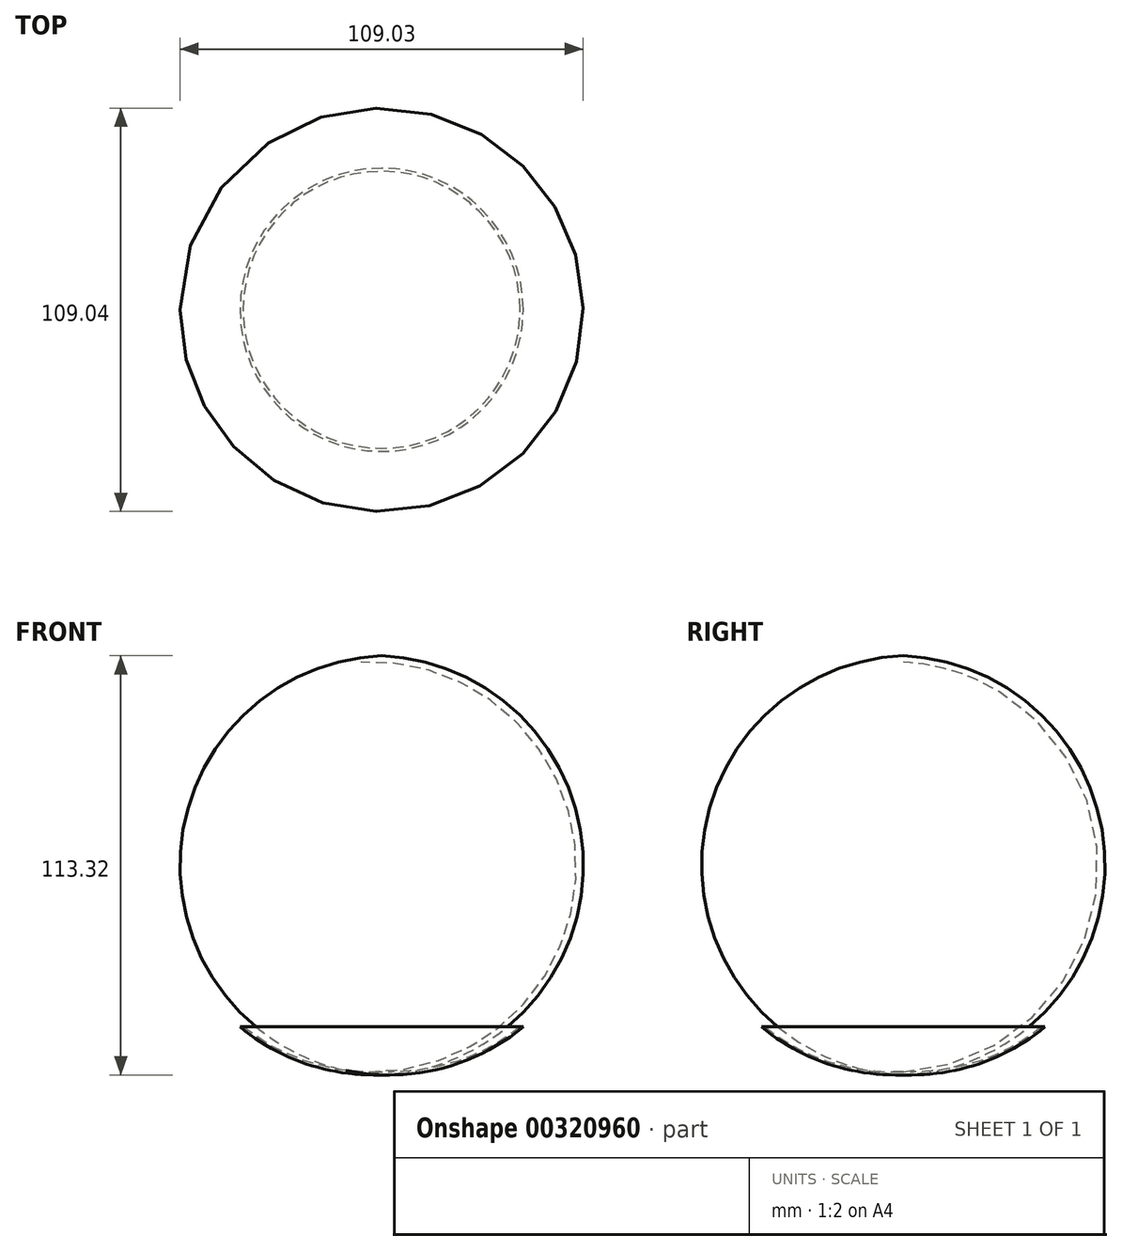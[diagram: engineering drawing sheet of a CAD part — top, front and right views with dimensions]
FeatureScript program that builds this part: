
annotation { "Feature Type Name" : "Feature", "Feature Type Description" : "" }
export const myFeature = defineFeature(function(context is Context, id is Id, definition is map)
    precondition{}
    {
        {
            var Q0;
            Q0=qCreatedBy(makeId("Front.planeOp"),FACE);
            var sketch = newSketch(context, id + "F0", { "sketchPlane" : qUnion([Q0])});
            skLineSegment(sketch, "E0", {"start": v(-76.27, 0) * mm, "end": v(-38, 0) * mm});
            skLineSegment(sketch, "E1", {"start": v(-38, 0) * mm, "end": v(-38, -12.95) * mm});
            skArc(sketch, "E2", {"start": v(-76.27, 0) * mm, "mid": v(-58.32, -10) * mm, "end": v(-38, -12.95) * mm});
            skSolve(sketch);
        }
        {
            var Q0;
            Q0 = qSketchRegion(id + "F0", true);
            var Q1;
            Q1=sQuery(id+"F0.wireOp",EDGE,"E1");
            revolve(context, id + "F1", {"entities" : qUnion([Q0]), "axis" : qUnion([Q1]), "revolveType" : RevolveType.FULL});
        }
        {
            var Q0;
            Q0=qCreatedBy(makeId("Front.planeOp"),FACE);
            var sketch = newSketch(context, id + "F2", { "sketchPlane" : qUnion([Q0])});
            skLineSegment(sketch, "E3", {"start": v(-38.02, 0) * mm, "end": v(-38.02, -12.1) * mm});
            skLineSegment(sketch, "E4", {"start": v(-38.02, 0) * mm, "end": v(-75.46, 0) * mm});
            skArc(sketch, "E5", {"start": v(-75.46, 0) * mm, "mid": v(-57.85, -9.49) * mm, "end": v(-38.02, -12.1) * mm});
            skSolve(sketch);
        }
        {
            var Q0;
            Q0 = qSketchRegion(id + "F2", true);
            var Q1;
            Q1=sQuery(id+"F2.wireOp",EDGE,"E3");
            revolve(context, id + "F3", {"operationType" : NewBodyOperationType.REMOVE, "entities" : qUnion([Q0]), "axis" : qUnion([Q1]), "revolveType" : RevolveType.FULL, "oppositeDirection" : true});
        }
    });
